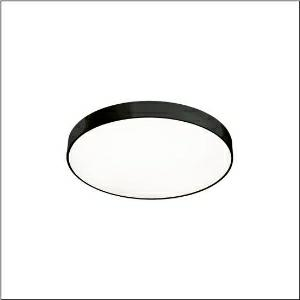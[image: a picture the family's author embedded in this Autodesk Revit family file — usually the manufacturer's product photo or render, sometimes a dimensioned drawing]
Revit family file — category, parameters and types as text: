
# Revit family: round_21_m_51mr36gm8421b
name_source: partatom
category: Lighting Fixtures
units: mm (PartAtom-declared; Revit-internal decimal feet)

## family parameters
Cut with Voids When Loaded = No
Host = Face
Light Source = No
Part Type = Normal
Room Calculation Point = No
Round Connector Dimension = Use Diameter
Shared = No

## types (1)
- --- (1 x LED, 8960 lm, 62.3 W, 4000K)
    Apparent Load = 62 VA
    CIE Flux Codes = 49 80 96 85 100
    Color Rendering = 80
    Color Temperature = 4000K
    Default Elevation = 1800 mm
    Description = Round 21 M, wall and ceiling luminaire, primary optical cover: cover, of PMMA, opal, light emission: direct/indirect distribution, primary light characteristic: symmetric, installation type: suspended mounting, surface-mounted, LED, rated luminous flux: 8.190lm, luminous efficacy: 135lm/W, light colour: 840, colour temperature: 4000K, control gear: ON/OFF Multilumen, with terminal, 3-pole, mains connection: 230V, AC, 50/60Hz, rated input power: 61W, housing, of aluminium, coated, black, diameter: 600mm, height: 62mm, protection rating (complete): IP40, insulation class (complete): insulation class I (protective earthing), certification: CE, impact resistance: IK04, permissible operating ambient temperature: -10..+35°C, packaging unit: 1 piece
    Height = 87 mm
    Lamp = 1 x LED
    Lamp Light Flux = 8960 lm
    Lamp Power = 62.3 W
    Lamp count = 1
    Length = 600 mm
    Luminous efficacy = 144 lm/W
    Manufacturer = Siteco
    ModVariant = No
    Model = 51MR36GM8421B
    Mounting Place = Ceiling
    Mounting Type = Surface mounted
    Number of Poles = 1
    OnlyDefault = Yes
    Power Factor = 1
    Product Name = Round 21 M
    Product group = wall and ceiling luminaire | ceiling mounted
    ProductGroupID = 304
    Protection Class = Protection class I
    Protection Degree = IP 40
    RLX_Detail_Level = 1
    RLX_Emergency_Light_Flux = 0 lm
    RLX_Emergency_Type = 0
    RLX_Emergency_Type_DB = No
    RlxData = <blob elided: 20869 chars, md5=94eb899d>
    Socket = socket
    Standby Power = 0 W
    System Light Flux = 8960 lm
    System Power = 62 W
    Type Comments = factory setting: luminous flux: 100 % | (ON | ON | ON | ON) | 700 mA
    Type Image = l_1258332.jpg
    URL = http://relux.com
    VarID = @adj_039289
    Voltage = 0 V
    Weight = 0.00 kg
    Width = 0 mm  [stored 0 ft]

note: [stored X ft] marks values corroborated as IEEE doubles in the binary element streams (Revit-internal decimal feet)

## geometry (parser evidence)
native form markers: Blend x4, Sweep x12
no freeform markers — native parametric forms only
